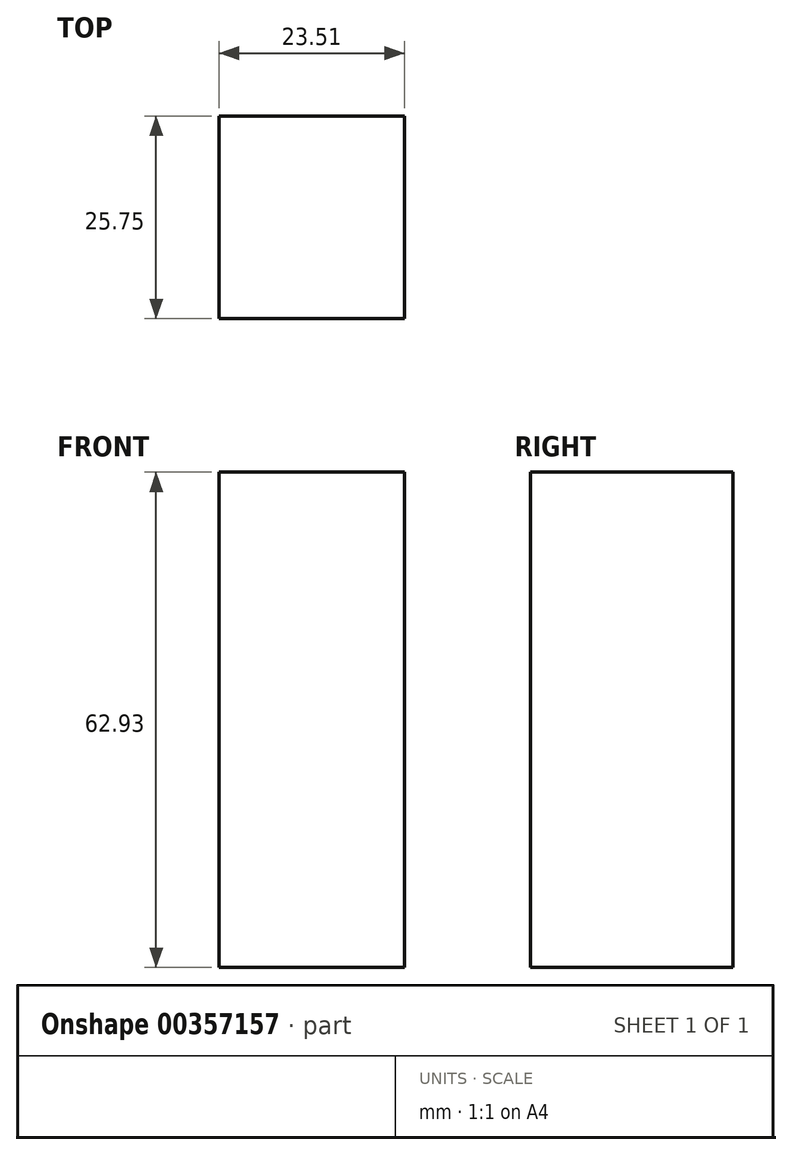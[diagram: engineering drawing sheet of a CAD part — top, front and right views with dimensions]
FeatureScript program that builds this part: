
annotation { "Feature Type Name" : "Feature", "Feature Type Description" : "" }
export const myFeature = defineFeature(function(context is Context, id is Id, definition is map)
    precondition{}
    {
        {
            var Q0;
            Q0=qCreatedBy(makeId("Top.planeOp"),FACE);
            var sketch = newSketch(context, id + "F0", { "sketchPlane" : qUnion([Q0])});
            skLineSegment(sketch, "E0.bottom", {"start": v(42.95, -54.15) * mm, "end": v(19.44, -54.15) * mm});
            skLineSegment(sketch, "E0.top", {"start": v(42.95, -28.4) * mm, "end": v(19.44, -28.4) * mm});
            skLineSegment(sketch, "E0.left", {"start": v(42.95, -54.15) * mm, "end": v(42.95, -28.4) * mm});
            skLineSegment(sketch, "E0.right", {"start": v(19.44, -54.15) * mm, "end": v(19.44, -28.4) * mm});
            skSolve(sketch);
        }
        {
            var Q0;
            Q0=makeQuery(id+"F0.imprint","IMPRINT",FACE,{"disambiguationData":[TD([[makeQuery(id+"F0.imprint","IMPRINT",EDGE,{"derivedFrom":sQuery(id+"F0.wireOp",EDGE,"E0.bottom")}),-1.0]])]});
            var sketch = newSketch(context, id + "F1", { "sketchPlane" : qUnion([Q0])});
            skSolve(sketch);
        }
        {
            var Q0;
            Q0 = qSketchRegion(id + "F1", true);
            var Q1;
            Q1=makeQuery(id+"F1.imprint","IMPRINT",FACE,{"disambiguationData":[TD([[makeQuery(id+"F1.imprint","IMPRINT",EDGE,{"derivedFrom":makeQuery(id+"F0.imprint","IMPRINT",EDGE,{"derivedFrom":sQuery(id+"F0.wireOp",EDGE,"E0.bottom")})}),-1.0]])]});
            extrude(context, id + "F2", {"entities" : qUnion([Q0, Q1]), "depth" : 62.93 * mm});
        }
    });
